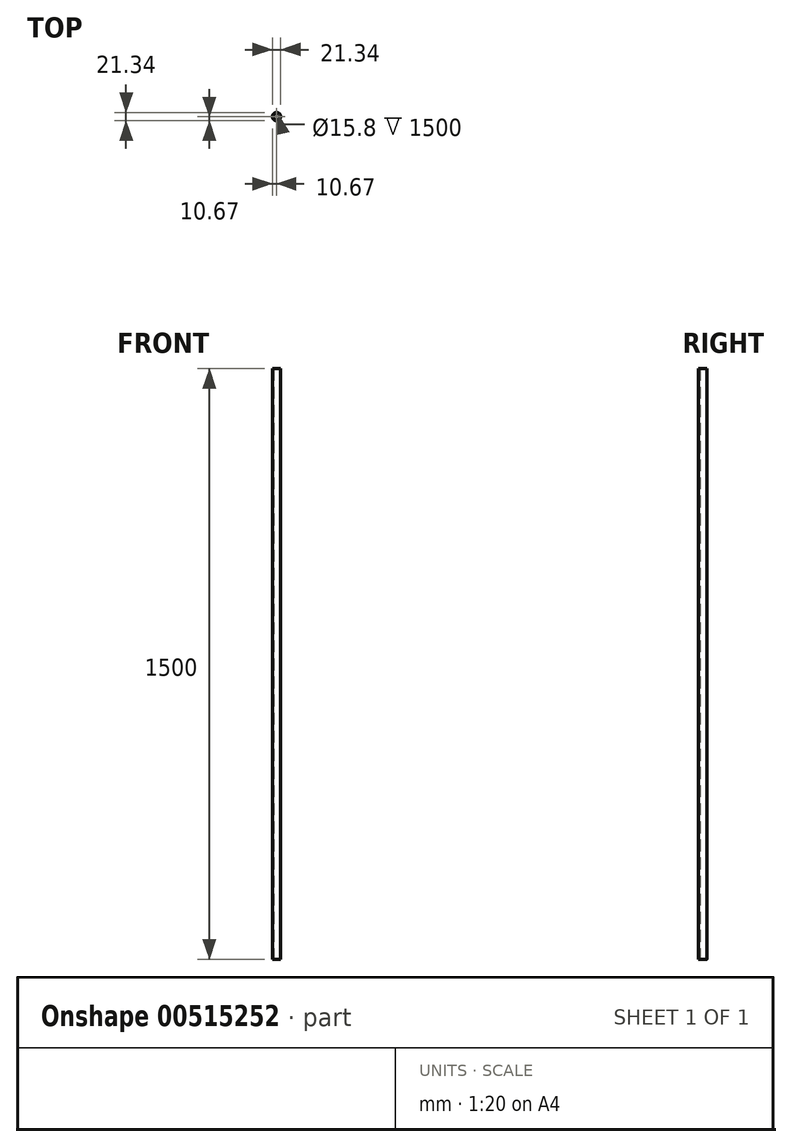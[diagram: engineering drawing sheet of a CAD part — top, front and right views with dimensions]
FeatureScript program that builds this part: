
annotation { "Feature Type Name" : "Feature", "Feature Type Description" : "" }
export const myFeature = defineFeature(function(context is Context, id is Id, definition is map)
    precondition{}
    {
        {
            var Q0;
            Q0=qCreatedBy(makeId("Top.planeOp"),FACE);
            var sketch = newSketch(context, id + "F0", { "sketchPlane" : qUnion([Q0])});
            skCircle(sketch, "E0", {"center": v(0, 0) * mm, "radius": 10.67 * mm});
            skSolve(sketch);
        }
        {
            var Q0;
            Q0=makeQuery(id+"F0.imprint","IMPRINT",FACE,{"disambiguationData":[TD([[makeQuery(id+"F0.imprint","IMPRINT",EDGE,{"derivedFrom":sQuery(id+"F0.wireOp",EDGE,"E0")}),1.0]])]});
            extrude(context, id + "F1", {"entities" : qUnion([Q0]), "depth" : 1500 * mm, "offsetDistance" : 25 * mm});
        }
        {
            var Q0;
            Q0=makeQuery(id+"F1.opExtrude","CAP_FACE",FACE,{"disambiguationData":[OSD([sQuery(id+"F0.wireOp",EDGE,"E0")])],"isStart":false});
            var Q1;
            Q1=makeQuery(id+"F1.opExtrude","CAP_FACE",FACE,{"disambiguationData":[OSD([sQuery(id+"F0.wireOp",EDGE,"E0")])],"isStart":true});
            var Q2;
            Q2=makeQuery(id+"F1.opExtrude","SWEPT_BODY",BODY,{"disambiguationData":[OSD([sQuery(id+"F0.wireOp",EDGE,"E0")])]});
            shell(context, id + "F2", {"entities" : qUnion([Q0, Q1]), "parts" : qUnion([Q2]), "thickness" : (.109 * 25.4) * mm});
        }
    });
